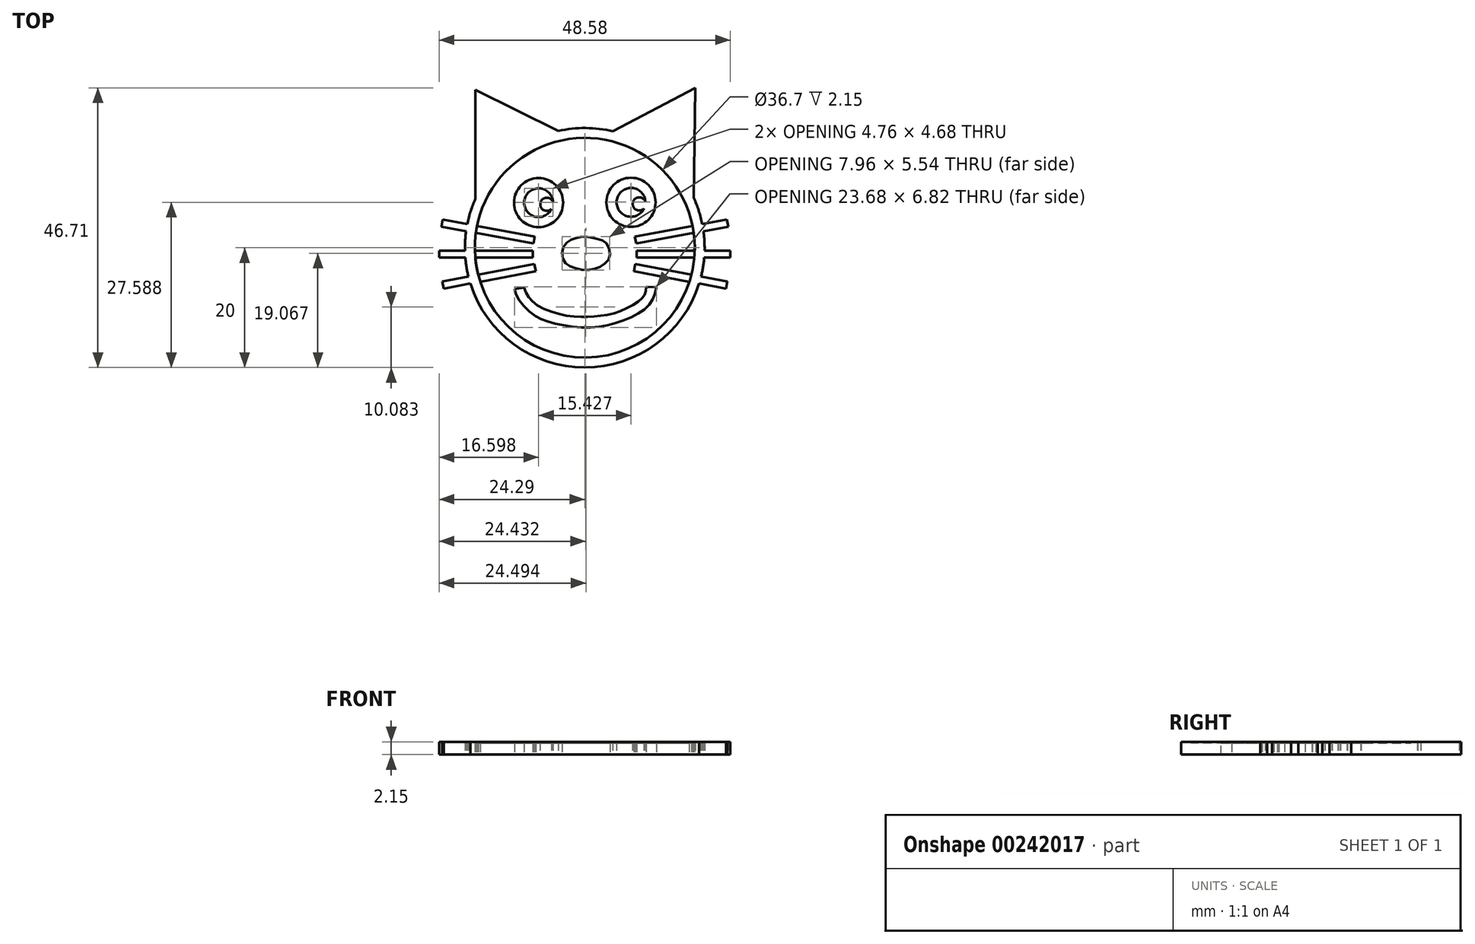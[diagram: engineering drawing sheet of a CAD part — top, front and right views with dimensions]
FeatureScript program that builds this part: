
annotation { "Feature Type Name" : "Feature", "Feature Type Description" : "" }
export const myFeature = defineFeature(function(context is Context, id is Id, definition is map)
    precondition{}
    {
        {
            var Q0;
            Q0=qCreatedBy(makeId("Top.planeOp"),FACE);
            var sketch = newSketch(context, id + "F0", { "sketchPlane" : qUnion([Q0])});
            skCircle(sketch, "E0", {"center": v(0, 0) * mm, "radius": 20 * mm});
            skPoint(sketch, "E0.first.point", {"position": v(-14.37, -13.91) * mm});
            skPoint(sketch, "E0.second.point", {"position": v(18.58, 7.4) * mm});
            skPoint(sketch, "E0.third.point", {"position": v(0, -20) * mm});
            skLineSegment(sketch, "E1", {"start": v(-8.66, -1.66) * mm, "end": v(-24.3, -1.66) * mm});
            skLineSegment(sketch, "E2", {"start": v(-24.3, -1.66) * mm, "end": v(-24.3, -0.46) * mm});
            skLineSegment(sketch, "E3", {"start": v(-24.3, -0.46) * mm, "end": v(-8.66, -0.46) * mm});
            skLineSegment(sketch, "E4", {"start": v(-8.66, -0.46) * mm, "end": v(-8.66, -1.66) * mm});
            skLineSegment(sketch, "E5", {"start": v(-8.57, 0.7) * mm, "end": v(-23.94, 3.54) * mm});
            skLineSegment(sketch, "E6", {"start": v(-23.94, 3.54) * mm, "end": v(-23.72, 4.72) * mm});
            skLineSegment(sketch, "E7", {"start": v(-23.72, 4.72) * mm, "end": v(-8.35, 1.89) * mm});
            skLineSegment(sketch, "E8", {"start": v(-8.35, 1.89) * mm, "end": v(-8.57, 0.7) * mm});
            skLineSegment(sketch, "E9.0", {"start": v(-8.57, 0.7) * mm, "end": v(-8.35, 1.89) * mm});
            skLineSegment(sketch, "E10", {"start": v(-8.2, -3.92) * mm, "end": v(-23.55, -6.82) * mm});
            skLineSegment(sketch, "E11", {"start": v(-23.55, -6.82) * mm, "end": v(-23.78, -5.65) * mm});
            skLineSegment(sketch, "E12", {"start": v(-23.78, -5.65) * mm, "end": v(-8.42, -2.74) * mm});
            skLineSegment(sketch, "E13", {"start": v(-8.42, -2.74) * mm, "end": v(-8.2, -3.92) * mm});
            skLineSegment(sketch, "E14.0", {"start": v(-8.2, -3.92) * mm, "end": v(-8.42, -2.74) * mm});
            skLineSegment(sketch, "E15", {"start": v(-18.23, 8.22) * mm, "end": v(-18.23, 26.37) * mm});
            skLineSegment(sketch, "E16", {"start": v(-18.23, 26.37) * mm, "end": v(-4.44, 19.5) * mm});
            skCircle(sketch, "E17", {"center": v(-7.71, 7.53) * mm, "radius": 4.1 * mm});
            skPoint(sketch, "E17.first.point", {"position": v(-10.97, 10.03) * mm});
            skPoint(sketch, "E17.second.point", {"position": v(-4.07, 9.41) * mm});
            skPoint(sketch, "E17.third.point", {"position": v(-7.54, 3.43) * mm});
            skCircle(sketch, "E18.0", {"center": v(-7.71, 7.53) * mm, "radius": 2.4 * mm});
            skCircle(sketch, "E19", {"center": v(-6.33, 7.27) * mm, "radius": 1.1 * mm});
            skCircle(sketch, "E20", {"center": v(7.71, 7.59) * mm, "radius": 4.1 * mm});
            skCircle(sketch, "E21.0", {"center": v(7.71, 7.59) * mm, "radius": 2.4 * mm});
            skCircle(sketch, "E22", {"center": v(9.1, 7.32) * mm, "radius": 1.1 * mm});
            skFitSpline(sketch, "E23", {"points": [v(-10.16, -6.66) * mm, v(-9.09, -8.6) * mm, v(-6.02, -10.55) * mm, v(-1.37, -11.52) * mm, v(2, -11.42) * mm, v(5.54, -10.75) * mm, v(8.76, -9.07) * mm, v(9.99, -7.84) * mm, v(10.24, -6.5) * mm], "startDerivative": vector(7.5, -18.42) * mm, "endDerivative": vector(1.11, 16.43) * mm});
            skFitSpline(sketch, "E24", {"points": [v(-11.7, -6.92) * mm, v(-10.98, -8.76) * mm, v(-8.58, -11.16) * mm, v(-6.22, -12.29) * mm, v(-2.29, -13.16) * mm, v(2.32, -13.2) * mm, v(6.2, -12.24) * mm, v(9.47, -10.65) * mm, v(11.21, -8.86) * mm, v(11.98, -6.56) * mm], "startDerivative": vector(5.23, -20.46) * mm, "endDerivative": vector(5.92, 24.95) * mm});
            skLineSegment(sketch, "E25", {"start": v(-11.7, -6.92) * mm, "end": v(-10.16, -6.66) * mm});
            skLineSegment(sketch, "E26", {"start": v(10.24, -6.5) * mm, "end": v(11.98, -6.56) * mm});
            skFitSpline(sketch, "E27", {"points": [v(0, 1.84) * mm, v(-1.26, 1.67) * mm, v(-2.75, 1.11) * mm, v(-3.77, -0.58) * mm, v(-3.3, -2.47) * mm, v(-1.67, -3.39) * mm, v(0.78, -3.7) * mm, v(2.98, -2.93) * mm, v(4.16, -1.5) * mm, v(3.64, 0.65) * mm, v(2.37, 1.42) * mm, v(0, 1.84) * mm]});
            skLineSegment(sketch, "E28", {"start": v(4.7, 19.44) * mm, "end": v(18.46, 26.7) * mm});
            skLineSegment(sketch, "E29", {"start": v(18.46, 26.7) * mm, "end": v(18.18, 8.34) * mm});
            skLineSegment(sketch, "E30.MirrorCS", {"start": v(23.55, -6.82) * mm, "end": v(23.78, -5.65) * mm});
            skLineSegment(sketch, "E31.MirrorCS", {"start": v(24.3, -1.66) * mm, "end": v(24.3, -0.46) * mm});
            skLineSegment(sketch, "E32.MirrorCS", {"start": v(23.94, 3.54) * mm, "end": v(23.72, 4.72) * mm});
            skLineSegment(sketch, "E33.MirrorCS", {"start": v(8.2, -3.92) * mm, "end": v(23.55, -6.82) * mm});
            skLineSegment(sketch, "E34.MirrorCS", {"start": v(23.78, -5.65) * mm, "end": v(8.42, -2.74) * mm});
            skLineSegment(sketch, "E35.MirrorCS", {"start": v(8.66, -1.66) * mm, "end": v(24.3, -1.66) * mm});
            skLineSegment(sketch, "E36.MirrorCS", {"start": v(24.3, -0.46) * mm, "end": v(8.66, -0.46) * mm});
            skLineSegment(sketch, "E37.MirrorCS", {"start": v(8.57, 0.7) * mm, "end": v(23.94, 3.54) * mm});
            skLineSegment(sketch, "E38.MirrorCS", {"start": v(23.72, 4.72) * mm, "end": v(8.35, 1.89) * mm});
            skLineSegment(sketch, "E39.MirrorCS", {"start": v(8.66, -0.46) * mm, "end": v(8.66, -1.66) * mm});
            skLineSegment(sketch, "E40.MirrorCS", {"start": v(8.2, -3.92) * mm, "end": v(8.42, -2.74) * mm});
            skLineSegment(sketch, "E41.MirrorCS", {"start": v(8.57, 0.7) * mm, "end": v(8.35, 1.89) * mm});
            skCircle(sketch, "E42", {"center": v(0, 0) * mm, "radius": 18.35 * mm});
            skSolve(sketch);
        }
        {
            var Q0;
            {var subQ0=sQuery(id+"F0.wireOp",EDGE,"E15");Q0=makeQuery(id+"F0.imprint","IMPRINT",FACE,{"disambiguationData":[TD([[makeQuery(id+"F0.imprint","IMPRINT",EDGE,{"derivedFrom":subQ0}),-1.0]])]});}
            var Q1;
            {var subQ0=sQuery(id+"F0.wireOp",EDGE,"E0");var subQ4=makeQuery(id+"F0.imprint","INTERSECT",VERTEX,{"derivedFrom":[subQ0,sQuery(id+"F0.wireOp",EDGE,"E29")]});Q1=makeQuery(id+"F0.imprint","IMPRINT",FACE,{"disambiguationData":[TD([[makeQuery(id+"F0.imprint","IMPRINT",EDGE,{"disambiguationData":[TD([[subQ4,1.0]])],"derivedFrom":subQ0}),1.0]])]});}
            var Q2;
            {var subQ0=sQuery(id+"F0.wireOp",EDGE,"E28");Q2=makeQuery(id+"F0.imprint","IMPRINT",FACE,{"disambiguationData":[TD([[makeQuery(id+"F0.imprint","IMPRINT",EDGE,{"derivedFrom":subQ0}),-1.0]])]});}
            var Q3;
            {var subQ0=sQuery(id+"F0.wireOp",EDGE,"E5");var subQ1=sQuery(id+"F0.wireOp",EDGE,"E0");var subQ2=makeQuery(id+"F0.imprint","INTERSECT",VERTEX,{"derivedFrom":[subQ1,subQ0]});Q3=makeQuery(id+"F0.imprint","IMPRINT",FACE,{"disambiguationData":[TD([[makeQuery(id+"F0.imprint","IMPRINT",EDGE,{"disambiguationData":[TD([[subQ2,-1.0]])],"derivedFrom":subQ1}),1.0]])]});}
            var Q4;
            {var subQ5=sQuery(id+"F0.wireOp",EDGE,"E6");Q4=makeQuery(id+"F0.imprint","IMPRINT",FACE,{"disambiguationData":[TD([[makeQuery(id+"F0.imprint","IMPRINT",EDGE,{"derivedFrom":subQ5}),-1.0]])]});}
            var Q5;
            {var subQ0=sQuery(id+"F0.wireOp",EDGE,"E7");var subQ1=sQuery(id+"F0.wireOp",EDGE,"E0");var subQ2=makeQuery(id+"F0.imprint","INTERSECT",VERTEX,{"derivedFrom":[subQ1,subQ0]});Q5=makeQuery(id+"F0.imprint","IMPRINT",FACE,{"disambiguationData":[TD([[makeQuery(id+"F0.imprint","IMPRINT",EDGE,{"disambiguationData":[TD([[subQ2,-1.0]])],"derivedFrom":subQ1}),1.0]])]});}
            var Q6;
            {var subQ0=sQuery(id+"F0.wireOp",EDGE,"E3");var subQ1=sQuery(id+"F0.wireOp",EDGE,"E0");var subQ2=makeQuery(id+"F0.imprint","INTERSECT",VERTEX,{"derivedFrom":[subQ1,subQ0]});Q6=makeQuery(id+"F0.imprint","IMPRINT",FACE,{"disambiguationData":[TD([[makeQuery(id+"F0.imprint","IMPRINT",EDGE,{"disambiguationData":[TD([[subQ2,-1.0]])],"derivedFrom":subQ1}),1.0]])]});}
            var Q7;
            {var subQ5=sQuery(id+"F0.wireOp",EDGE,"E2");Q7=makeQuery(id+"F0.imprint","IMPRINT",FACE,{"disambiguationData":[TD([[makeQuery(id+"F0.imprint","IMPRINT",EDGE,{"derivedFrom":subQ5}),-1.0]])]});}
            var Q8;
            {var subQ5=sQuery(id+"F0.wireOp",EDGE,"E11");Q8=makeQuery(id+"F0.imprint","IMPRINT",FACE,{"disambiguationData":[TD([[makeQuery(id+"F0.imprint","IMPRINT",EDGE,{"derivedFrom":subQ5}),-1.0]])]});}
            var Q9;
            {var subQ0=sQuery(id+"F0.wireOp",EDGE,"E12");var subQ1=sQuery(id+"F0.wireOp",EDGE,"E0");var subQ2=makeQuery(id+"F0.imprint","INTERSECT",VERTEX,{"derivedFrom":[subQ1,subQ0]});Q9=makeQuery(id+"F0.imprint","IMPRINT",FACE,{"disambiguationData":[TD([[makeQuery(id+"F0.imprint","IMPRINT",EDGE,{"disambiguationData":[TD([[subQ2,-1.0]])],"derivedFrom":subQ1}),1.0]])]});}
            var Q10;
            {var subQ0=sQuery(id+"F0.wireOp",EDGE,"E1");var subQ1=sQuery(id+"F0.wireOp",EDGE,"E0");var subQ2=makeQuery(id+"F0.imprint","INTERSECT",VERTEX,{"derivedFrom":[subQ1,subQ0]});Q10=makeQuery(id+"F0.imprint","IMPRINT",FACE,{"disambiguationData":[TD([[makeQuery(id+"F0.imprint","IMPRINT",EDGE,{"disambiguationData":[TD([[subQ2,-1.0]])],"derivedFrom":subQ1}),1.0]])]});}
            var Q11;
            {var subQ0=sQuery(id+"F0.wireOp",EDGE,"E10");var subQ1=sQuery(id+"F0.wireOp",EDGE,"E0");var subQ2=makeQuery(id+"F0.imprint","INTERSECT",VERTEX,{"derivedFrom":[subQ1,subQ0]});Q11=makeQuery(id+"F0.imprint","IMPRINT",FACE,{"disambiguationData":[TD([[makeQuery(id+"F0.imprint","IMPRINT",EDGE,{"disambiguationData":[TD([[subQ2,-1.0]])],"derivedFrom":subQ1}),1.0]])]});}
            var Q12;
            {var subQ0=sQuery(id+"F0.wireOp",EDGE,"E34.MirrorCS");var subQ1=sQuery(id+"F0.wireOp",EDGE,"E0");var subQ2=makeQuery(id+"F0.imprint","INTERSECT",VERTEX,{"derivedFrom":[subQ1,subQ0]});Q12=makeQuery(id+"F0.imprint","IMPRINT",FACE,{"disambiguationData":[TD([[makeQuery(id+"F0.imprint","IMPRINT",EDGE,{"disambiguationData":[TD([[subQ2,-1.0]])],"derivedFrom":subQ1}),1.0]])]});}
            var Q13;
            {var subQ0=sQuery(id+"F0.wireOp",EDGE,"E33.MirrorCS");var subQ1=sQuery(id+"F0.wireOp",EDGE,"E0");var subQ2=makeQuery(id+"F0.imprint","INTERSECT",VERTEX,{"derivedFrom":[subQ1,subQ0]});Q13=makeQuery(id+"F0.imprint","IMPRINT",FACE,{"disambiguationData":[TD([[makeQuery(id+"F0.imprint","IMPRINT",EDGE,{"disambiguationData":[TD([[subQ2,-1.0]])],"derivedFrom":subQ1}),1.0]])]});}
            var Q14;
            {var subQ5=sQuery(id+"F0.wireOp",EDGE,"E30.MirrorCS");Q14=makeQuery(id+"F0.imprint","IMPRINT",FACE,{"disambiguationData":[TD([[makeQuery(id+"F0.imprint","IMPRINT",EDGE,{"derivedFrom":subQ5}),1.0]])]});}
            var Q15;
            {var subQ5=sQuery(id+"F0.wireOp",EDGE,"E31.MirrorCS");Q15=makeQuery(id+"F0.imprint","IMPRINT",FACE,{"disambiguationData":[TD([[makeQuery(id+"F0.imprint","IMPRINT",EDGE,{"derivedFrom":subQ5}),1.0]])]});}
            var Q16;
            {var subQ0=sQuery(id+"F0.wireOp",EDGE,"E35.MirrorCS");var subQ1=sQuery(id+"F0.wireOp",EDGE,"E0");var subQ2=makeQuery(id+"F0.imprint","INTERSECT",VERTEX,{"derivedFrom":[subQ1,subQ0]});Q16=makeQuery(id+"F0.imprint","IMPRINT",FACE,{"disambiguationData":[TD([[makeQuery(id+"F0.imprint","IMPRINT",EDGE,{"disambiguationData":[TD([[subQ2,-1.0]])],"derivedFrom":subQ1}),1.0]])]});}
            var Q17;
            {var subQ0=sQuery(id+"F0.wireOp",EDGE,"E37.MirrorCS");var subQ1=sQuery(id+"F0.wireOp",EDGE,"E0");var subQ2=makeQuery(id+"F0.imprint","INTERSECT",VERTEX,{"derivedFrom":[subQ1,subQ0]});Q17=makeQuery(id+"F0.imprint","IMPRINT",FACE,{"disambiguationData":[TD([[makeQuery(id+"F0.imprint","IMPRINT",EDGE,{"disambiguationData":[TD([[subQ2,1.0]])],"derivedFrom":subQ1}),1.0]])]});}
            var Q18;
            {var subQ5=sQuery(id+"F0.wireOp",EDGE,"E32.MirrorCS");Q18=makeQuery(id+"F0.imprint","IMPRINT",FACE,{"disambiguationData":[TD([[makeQuery(id+"F0.imprint","IMPRINT",EDGE,{"derivedFrom":subQ5}),1.0]])]});}
            var Q19;
            {var subQ0=sQuery(id+"F0.wireOp",EDGE,"E38.MirrorCS");var subQ1=sQuery(id+"F0.wireOp",EDGE,"E0");var subQ2=makeQuery(id+"F0.imprint","INTERSECT",VERTEX,{"derivedFrom":[subQ1,subQ0]});Q19=makeQuery(id+"F0.imprint","IMPRINT",FACE,{"disambiguationData":[TD([[makeQuery(id+"F0.imprint","IMPRINT",EDGE,{"disambiguationData":[TD([[subQ2,1.0]])],"derivedFrom":subQ1}),1.0]])]});}
            var Q20;
            Q20=makeQuery(id+"F0.imprint","IMPRINT",FACE,{"disambiguationData":[TD([[makeQuery(id+"F0.imprint","IMPRINT",EDGE,{"derivedFrom":sQuery(id+"F0.wireOp",EDGE,"E17")}),1.0]])]});
            var Q21;
            Q21=makeQuery(id+"F0.imprint","IMPRINT",FACE,{"disambiguationData":[TD([[makeQuery(id+"F0.imprint","IMPRINT",EDGE,{"derivedFrom":sQuery(id+"F0.wireOp",EDGE,"E20")}),1.0]])]});
            var Q22;
            {var subQ0=sQuery(id+"F0.wireOp",EDGE,"E19");var subQ1=sQuery(id+"F0.wireOp",EDGE,"E18.0");var subQ2=makeQuery(id+"F0.imprint","INTERSECT",VERTEX,{"disambiguationData":[OD(0.0)],"derivedFrom":[subQ1,subQ0]});Q22=makeQuery(id+"F0.imprint","IMPRINT",FACE,{"disambiguationData":[TD([[makeQuery(id+"F0.imprint","IMPRINT",EDGE,{"disambiguationData":[TD([[subQ2,-1.0]])],"derivedFrom":subQ1}),1.0]])]});}
            var Q23;
            {var subQ0=sQuery(id+"F0.wireOp",EDGE,"E22");var subQ1=sQuery(id+"F0.wireOp",EDGE,"E21.0");var subQ2=makeQuery(id+"F0.imprint","INTERSECT",VERTEX,{"disambiguationData":[OD(0.0)],"derivedFrom":[subQ1,subQ0]});Q23=makeQuery(id+"F0.imprint","IMPRINT",FACE,{"disambiguationData":[TD([[makeQuery(id+"F0.imprint","IMPRINT",EDGE,{"disambiguationData":[TD([[subQ2,-1.0]])],"derivedFrom":subQ1}),1.0]])]});}
            var Q24;
            {var subQ0=sQuery(id+"F0.wireOp",EDGE,"E19");var subQ1=sQuery(id+"F0.wireOp",EDGE,"E18.0");var subQ2=makeQuery(id+"F0.imprint","INTERSECT",VERTEX,{"disambiguationData":[OD(0.0)],"derivedFrom":[subQ1,subQ0]});Q24=makeQuery(id+"F0.imprint","IMPRINT",FACE,{"disambiguationData":[TD([[makeQuery(id+"F0.imprint","IMPRINT",EDGE,{"disambiguationData":[TD([[subQ2,-1.0]])],"derivedFrom":subQ1}),-1.0]])]});}
            var Q25;
            {var subQ0=sQuery(id+"F0.wireOp",EDGE,"E22");var subQ1=sQuery(id+"F0.wireOp",EDGE,"E21.0");var subQ2=makeQuery(id+"F0.imprint","INTERSECT",VERTEX,{"disambiguationData":[OD(0.0)],"derivedFrom":[subQ1,subQ0]});Q25=makeQuery(id+"F0.imprint","IMPRINT",FACE,{"disambiguationData":[TD([[makeQuery(id+"F0.imprint","IMPRINT",EDGE,{"disambiguationData":[TD([[subQ2,-1.0]])],"derivedFrom":subQ1}),-1.0]])]});}
            extrude(context, id + "F1", {"entities" : qUnion([Q0, Q1, Q2, Q3, Q4, Q5, Q6, Q7, Q8, Q9, Q10, Q11, Q12, Q13, Q14, Q15, Q16, Q17, Q18, Q19, Q20, Q21, Q22, Q23, Q24, Q25]), "depth" : 2.15 * mm});
        }
        {
            var Q0;
            {var subQ26=sQuery(id+"F0.wireOp",EDGE,"E4");Q0=makeQuery(id+"F0.imprint","IMPRINT",FACE,{"disambiguationData":[TD([[makeQuery(id+"F0.imprint","IMPRINT",EDGE,{"derivedFrom":subQ26}),1.0]])]});}
            extrude(context, id + "F2", {"entities" : qUnion([Q0]), "depth" : 1.9 * mm});
        }
        {
            var Q0;
            Q0=makeQuery(id+"F1.opExtrude","SWEPT_BODY",BODY,{"disambiguationData":[OSD([sQuery(id+"F0.wireOp",EDGE,"E17"),sQuery(id+"F0.wireOp",EDGE,"E18.0"),sQuery(id+"F0.wireOp",EDGE,"E19")])]});
            var Q1;
            Q1=makeQuery(id+"F1.opExtrude","SWEPT_BODY",BODY,{"disambiguationData":[OSD([sQuery(id+"F0.wireOp",EDGE,"E0"),sQuery(id+"F0.wireOp",EDGE,"E1"),sQuery(id+"F0.wireOp",EDGE,"E2"),sQuery(id+"F0.wireOp",EDGE,"E3"),sQuery(id+"F0.wireOp",EDGE,"E5"),sQuery(id+"F0.wireOp",EDGE,"E6"),sQuery(id+"F0.wireOp",EDGE,"E7"),sQuery(id+"F0.wireOp",EDGE,"E10"),sQuery(id+"F0.wireOp",EDGE,"E11"),sQuery(id+"F0.wireOp",EDGE,"E12"),sQuery(id+"F0.wireOp",EDGE,"E15"),sQuery(id+"F0.wireOp",EDGE,"E16"),sQuery(id+"F0.wireOp",EDGE,"E28"),sQuery(id+"F0.wireOp",EDGE,"E29"),sQuery(id+"F0.wireOp",EDGE,"E30.MirrorCS"),sQuery(id+"F0.wireOp",EDGE,"E31.MirrorCS"),sQuery(id+"F0.wireOp",EDGE,"E32.MirrorCS"),sQuery(id+"F0.wireOp",EDGE,"E33.MirrorCS"),sQuery(id+"F0.wireOp",EDGE,"E34.MirrorCS"),sQuery(id+"F0.wireOp",EDGE,"E35.MirrorCS"),sQuery(id+"F0.wireOp",EDGE,"E36.MirrorCS"),sQuery(id+"F0.wireOp",EDGE,"E37.MirrorCS"),sQuery(id+"F0.wireOp",EDGE,"E38.MirrorCS"),sQuery(id+"F0.wireOp",EDGE,"E42")])]});
            var Q2;
            Q2=makeQuery(id+"F1.opExtrude","SWEPT_BODY",BODY,{"disambiguationData":[OSD([sQuery(id+"F0.wireOp",EDGE,"E20"),sQuery(id+"F0.wireOp",EDGE,"E21.0"),sQuery(id+"F0.wireOp",EDGE,"E22")])]});
            var Q3;
            Q3=makeQuery(id+"F2.opExtrude","SWEPT_BODY",BODY,{"disambiguationData":[OSD([sQuery(id+"F0.wireOp",EDGE,"E1"),sQuery(id+"F0.wireOp",EDGE,"E3"),sQuery(id+"F0.wireOp",EDGE,"E4"),sQuery(id+"F0.wireOp",EDGE,"E5"),sQuery(id+"F0.wireOp",EDGE,"E7"),sQuery(id+"F0.wireOp",EDGE,"E9.0"),sQuery(id+"F0.wireOp",EDGE,"E10"),sQuery(id+"F0.wireOp",EDGE,"E12"),sQuery(id+"F0.wireOp",EDGE,"E14.0"),sQuery(id+"F0.wireOp",EDGE,"E17"),sQuery(id+"F0.wireOp",EDGE,"E20"),sQuery(id+"F0.wireOp",EDGE,"E23"),sQuery(id+"F0.wireOp",EDGE,"E24"),sQuery(id+"F0.wireOp",EDGE,"E25"),sQuery(id+"F0.wireOp",EDGE,"E26"),sQuery(id+"F0.wireOp",EDGE,"E27"),sQuery(id+"F0.wireOp",EDGE,"E33.MirrorCS"),sQuery(id+"F0.wireOp",EDGE,"E34.MirrorCS"),sQuery(id+"F0.wireOp",EDGE,"E35.MirrorCS"),sQuery(id+"F0.wireOp",EDGE,"E36.MirrorCS"),sQuery(id+"F0.wireOp",EDGE,"E37.MirrorCS"),sQuery(id+"F0.wireOp",EDGE,"E38.MirrorCS"),sQuery(id+"F0.wireOp",EDGE,"E39.MirrorCS"),sQuery(id+"F0.wireOp",EDGE,"E40.MirrorCS"),sQuery(id+"F0.wireOp",EDGE,"E41.MirrorCS"),sQuery(id+"F0.wireOp",EDGE,"E42")])]});
            booleanBodies(context, id + "F3", {"operationType" : BooleanOperationType.UNION, "tools" : qUnion([Q0, Q1, Q2, Q3])});
        }
    });
